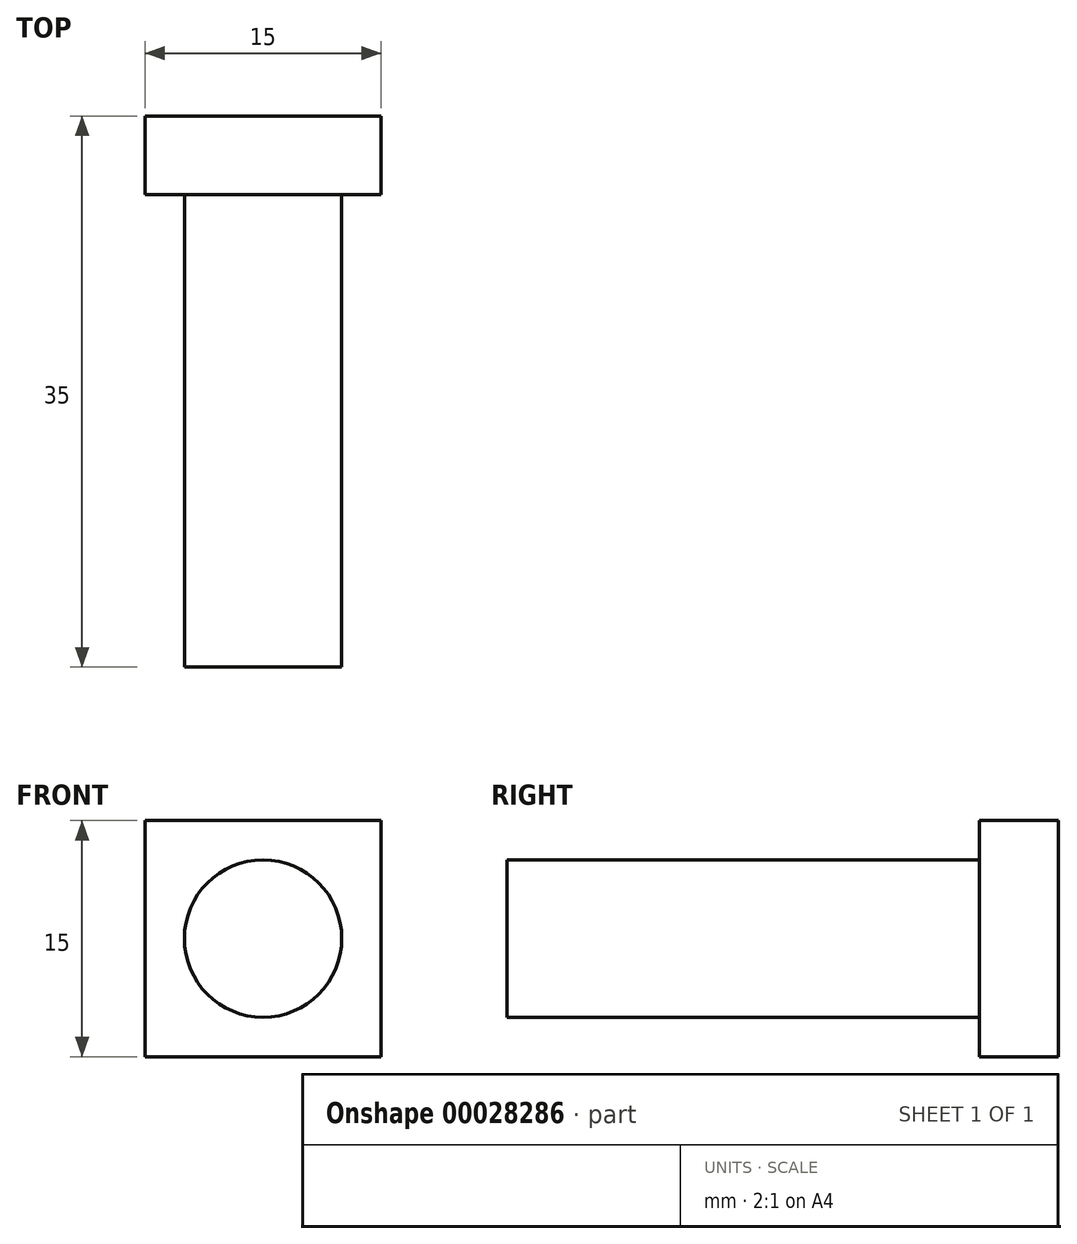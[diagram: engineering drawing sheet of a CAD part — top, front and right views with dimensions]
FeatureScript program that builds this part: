
annotation { "Feature Type Name" : "Feature", "Feature Type Description" : "" }
export const myFeature = defineFeature(function(context is Context, id is Id, definition is map)
    precondition{}
    {
        {
            var Q0;
            Q0=qCreatedBy(makeId("Front.planeOp"),FACE);
            var sketch = newSketch(context, id + "F0", { "sketchPlane" : qUnion([Q0])});
            skCircle(sketch, "E0", {"center": v(0, 0) * mm, "radius": 5 * mm});
            skSolve(sketch);
        }
        {
            var Q0;
            Q0=makeQuery(id+"F0.imprint","IMPRINT",FACE,{"disambiguationData":[TD([[makeQuery(id+"F0.imprint","IMPRINT",EDGE,{"derivedFrom":sQuery(id+"F0.wireOp",EDGE,"E0")}),1.0]])]});
            extrude(context, id + "F1", {"entities" : qUnion([Q0]), "depth" : 30 * mm});
        }
        {
            var Q0;
            Q0=makeQuery(id+"F1.opExtrude","CAP_FACE",FACE,{"disambiguationData":[OSD([sQuery(id+"F0.wireOp",EDGE,"E0")])],"isStart":true});
            var sketch = newSketch(context, id + "F2", { "sketchPlane" : qUnion([Q0])});
            skLineSegment(sketch, "E1.rect.bottom", {"start": v(7.5, -7.5) * mm, "end": v(-7.5, -7.5) * mm});
            skLineSegment(sketch, "E1.rect.top", {"start": v(7.5, 7.5) * mm, "end": v(-7.5, 7.5) * mm});
            skLineSegment(sketch, "E1.rect.left", {"start": v(7.5, -7.5) * mm, "end": v(7.5, 7.5) * mm});
            skLineSegment(sketch, "E1.rect.right", {"start": v(-7.5, -7.5) * mm, "end": v(-7.5, 7.5) * mm});
            skPoint(sketch, "E1.rect.middle", {"position": v(0, 0) * mm});
            skSolve(sketch);
        }
        {
            var Q0;
            Q0 = qSketchRegion(id + "F2", true);
            extrude(context, id + "F3", {"entities" : qUnion([Q0]), "operationType" : NewBodyOperationType.ADD, "depth" : 5 * mm});
        }
    });
